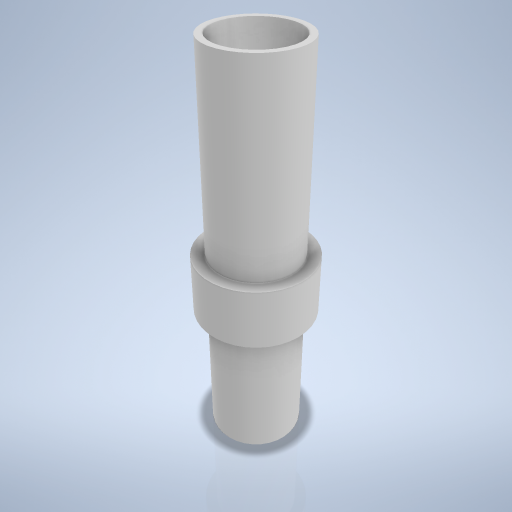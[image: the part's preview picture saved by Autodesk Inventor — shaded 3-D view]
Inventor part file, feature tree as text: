
AUTODESK INVENTOR PART (.ipt)
format: ipt  version: 2024.2 (Build 282272000, 272)  size: 267,776 bytes
history: native  units: mm
features: sketch x2, revolve x1, hole x1
ambient origin geometry x8: Origin, YZ Plane, XZ Plane, XY Plane, X Axis, Y Axis, Z Axis, Center Point
bodies: Volumenkörper1 (feature_tree)
feature tree (4):
  revolve  "Umdrehung1"
  hole  "Bohrung1"  [1 undecoded]
  sketch  "Skizze1"  dims[d0=14.056mm d1=21.0mm]
  sketch  "Skizze2"  dims[d2=27.0mm d4=90.0deg d5=18.0mm d6=6.0mm d7=4.0mm d8=2.0mm d9=90.0deg d10=8.0mm d11=20.594885mm d14=45.0mm d15=33.0mm]
note: 1 required parameter value undecoded (feature->parameter linkage not recoverable at this tier; creation-order binding heuristic only, values carry confidence <= 0.55)
